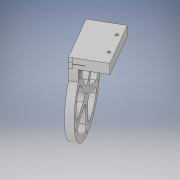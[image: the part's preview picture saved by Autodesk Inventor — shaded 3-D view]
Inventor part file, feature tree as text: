
AUTODESK INVENTOR PART (.ipt)
format: ipt  version: 2017 (Build 210142000, 142)  size: 359,424 bytes
history: native  units: in
note: dims shown in document units (in); Inventor stores cm internally (conversion verified against a paired STEP export)
features: extrude x10, sketch x10, projected_geometry x7, plane x1, imported_body x1
ambient origin geometry x8: Origin, YZ Plane, XZ Plane, XY Plane, X Axis, Y Axis, Z Axis, Center Point
bodies: Solid1 (feature_tree)
feature tree (29):
  extrude  "Extrusion1"  Depth=0.3937in TaperAngle=0.0deg
  extrude  "Extrusion2"  Depth=0.1969in
  extrude  "Extrusion3"  Depth=0.125in
  extrude  "Extrusion4"  Depth=0.3937in TaperAngle=0.0deg
  extrude  "Extrusion5"  Depth=0.7087in
  plane  "Work Plane1"
  extrude  "Extrusion6"  Depth=0.9154in
  extrude  "Extrusion7"  Depth=0.1969in
  extrude  "Extrusion8"  Depth=1.3091in
  extrude  "Extrusion9"  Depth=0.0787in TaperAngle=0.0deg
  extrude  "Extrusion10"  Depth=0.125in
  sketch  "Sketch1"  dims[d0=1.25in d1=0.0in d2=0.3937in d3=0.0in]
  projected_geometry  "Projected Loop1"
  projected_geometry  "Projected Loop2"
  projected_geometry  "Projected Loop3"
  sketch  "Sketch2"  dims[d4=0.1969in d5=0.0in d6=0.375in]
  sketch  "Sketch3"  dims[d7=0.5in d8=0.125in]
  projected_geometry  "Projected Loop4"
  sketch  "Sketch4"  dims[d9=0.3937in d10=0.0in d11=0.1875in d12=0.0in]
  sketch  "Sketch5"  dims[d13=3.2677in d19=0.7087in]
  projected_geometry  "Projected Loop5"
  sketch  "Sketch8"  dims[d20=0.6102in d21=0.9154in]
  sketch  "Sketch9"  dims[d22=0.6102in d23=0.1969in]
  sketch  "Sketch11"  dims[d24=0.0787in d25=1.3091in]
  sketch  "Sketch13"  dims[d26=0.6693in d27=0.0in d28=0.0787in d29=0.0in]
  projected_geometry  "Projected Loop8"
  sketch  "Sketch14"  dims[d30=0.0787in d31=0.0in d32=0.125in d33=0.0in d34=0.0787in d35=0.0in d36=0.0787in d37=90.0deg d38=0.5118in d39=0.0787in d40=0.0in]
  projected_geometry  "Projected Loop9"
  imported_body  "Base1"
